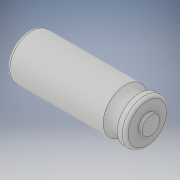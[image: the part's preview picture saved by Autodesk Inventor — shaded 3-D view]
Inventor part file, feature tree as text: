
AUTODESK INVENTOR PART (.ipt)
format: ipt  version: 2017 (Build 210142000, 142)  size: 137,728 bytes
history: native  units: in
note: dims shown in document units (in); Inventor stores cm internally (conversion verified against a paired STEP export)
features: sketch x2, revolve x1, extrude x1, fillet x1
ambient origin geometry x8: Origin, YZ Plane, XZ Plane, XY Plane, X Axis, Y Axis, Z Axis, Center Point
bodies: Solid1 (feature_tree)
feature tree (5):
  revolve  "Revolution1"  Angle=90.0deg
  extrude  "Extrusion1"  Depth=0.0625in TaperAngle=0.0deg
  fillet  "Fillet1"  Radius=0.05in
  sketch  "Sketch1"  dims[d1=0.375in d2=90.0deg]
  sketch  "Sketch2"  dims[d3=0.3in d4=0.0625in d5=0.0in d6=0.05in]
